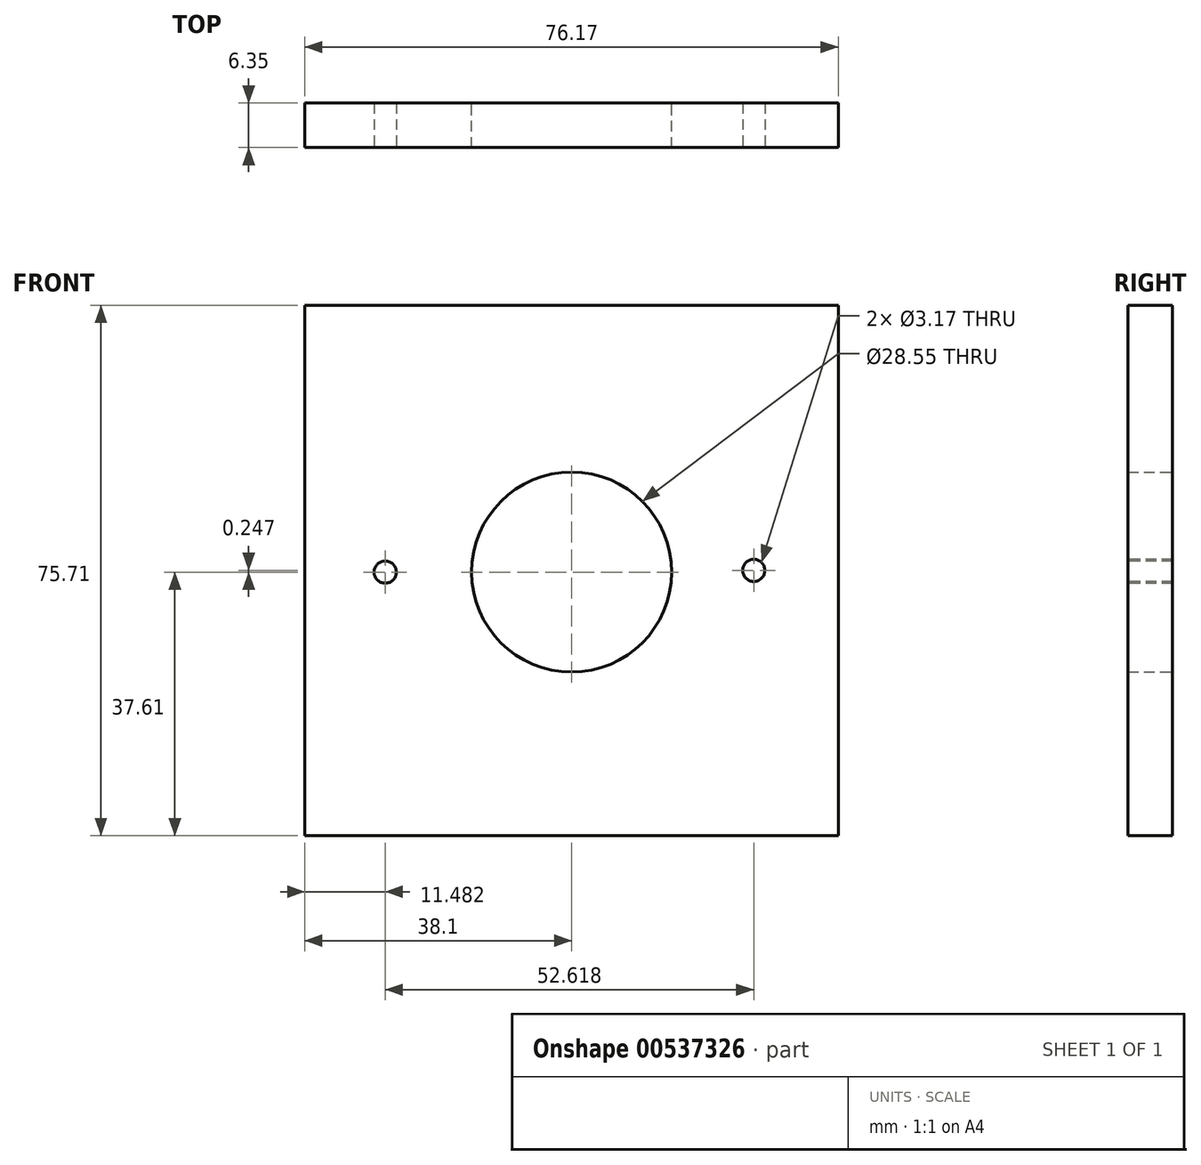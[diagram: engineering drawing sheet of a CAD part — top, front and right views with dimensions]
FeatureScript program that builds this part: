
annotation { "Feature Type Name" : "Feature", "Feature Type Description" : "" }
export const myFeature = defineFeature(function(context is Context, id is Id, definition is map)
    precondition{}
    {
        {
            var Q0;
            Q0=qCreatedBy(makeId("Front.planeOp"),FACE);
            var sketch = newSketch(context, id + "F0", { "sketchPlane" : qUnion([Q0])});
            skCircle(sketch, "E0", {"center": v(0, 0) * mm, "radius": 14.27 * mm});
            skLineSegment(sketch, "E1", {"start": v(-14.27, 0) * mm, "end": v(-38.1, 0) * mm, "construction": true});
            skLineSegment(sketch, "E2", {"start": v(14.27, 0) * mm, "end": v(38.1, 0) * mm, "construction": true});
            skLineSegment(sketch, "E3", {"start": v(0, 14.27) * mm, "end": v(0, 38.1) * mm, "construction": true});
            skLineSegment(sketch, "E4", {"start": v(0, -14.27) * mm, "end": v(0, -38.1) * mm, "construction": true});
            skLineSegment(sketch, "E5.bottom", {"start": v(-38.1, 38.1) * mm, "end": v(38.07, 38.1) * mm});
            skLineSegment(sketch, "E5.top", {"start": v(-38.1, -37.6) * mm, "end": v(38.07, -37.6) * mm});
            skLineSegment(sketch, "E5.left", {"start": v(-38.1, 38.1) * mm, "end": v(-38.1, -37.6) * mm});
            skLineSegment(sketch, "E5.right", {"start": v(38.07, 38.1) * mm, "end": v(38.07, -37.6) * mm});
            skSolve(sketch);
        }
        {
            var Q0;
            Q0=makeQuery(id+"F0.imprint","IMPRINT",FACE,{"disambiguationData":[TD([[makeQuery(id+"F0.imprint","IMPRINT",EDGE,{"derivedFrom":sQuery(id+"F0.wireOp",EDGE,"E0")}),-1.0]])]});
            extrude(context, id + "F1", {"entities" : qUnion([Q0]), "flatOperationType" : FlatOperationType.REMOVE, "depth" : 6.35 * mm, "offsetDistance" : 25.4 * mm, "domain" : OperationDomain.MODEL});
        }
        {
            var Q0;
            Q0=makeQuery(id+"F1.opExtrude","CAP_FACE",FACE,{"disambiguationData":[OSD([sQuery(id+"F0.wireOp",EDGE,"E0"),sQuery(id+"F0.wireOp",EDGE,"E5.bottom"),sQuery(id+"F0.wireOp",EDGE,"E5.top"),sQuery(id+"F0.wireOp",EDGE,"E5.left"),sQuery(id+"F0.wireOp",EDGE,"E5.right")])],"isStart":false});
            var sketch = newSketch(context, id + "F2", { "sketchPlane" : qUnion([Q0])});
            skLineSegment(sketch, "E6", {"start": v(-14.27, 0) * mm, "end": v(-24.6, 0) * mm});
            skPoint(sketch, "E7.startSnap0", {"position": v(-38.1, 0.25) * mm});
            skLineSegment(sketch, "E8", {"start": v(-27.77, 0.25) * mm, "end": v(-38.1, 0.25) * mm, "construction": true});
            skCircle(sketch, "E9", {"center": v(-26.62, 0) * mm, "radius": 1.59 * mm});
            skLineSegment(sketch, "E10", {"start": v(14.27, 0) * mm, "end": v(24.6, 0) * mm, "construction": true});
            skLineSegment(sketch, "E11", {"start": v(27.75, 0.25) * mm, "end": v(38.07, 0) * mm, "construction": true});
            skPoint(sketch, "E11.startSnap0", {"position": v(38.07, 0.25) * mm});
            skPoint(sketch, "E11.endSnap0", {"position": v(38.07, 0.25) * mm});
            skCircle(sketch, "E12", {"center": v(26.3, 0) * mm, "radius": 1.59 * mm});
            skSolve(sketch);
        }
        {
            var Q0;
            Q0=makeQuery(id+"F2.imprint","IMPRINT",FACE,{"disambiguationData":[TD([[makeQuery(id+"F2.imprint","IMPRINT",EDGE,{"derivedFrom":sQuery(id+"F2.wireOp",EDGE,"E9")}),1.0]])]});
            extrude(context, id + "F3", {"entities" : qUnion([Q0]), "operationType" : NewBodyOperationType.REMOVE, "oppositeDirection" : true, "depth" : 6.35 * mm, "offsetDistance" : 25.4 * mm});
        }
        {
            var Q0;
            Q0=makeQuery(id+"F1.opExtrude","CAP_FACE",FACE,{"disambiguationData":[OSD([sQuery(id+"F0.wireOp",EDGE,"E0"),sQuery(id+"F0.wireOp",EDGE,"E5.bottom"),sQuery(id+"F0.wireOp",EDGE,"E5.top"),sQuery(id+"F0.wireOp",EDGE,"E5.left"),sQuery(id+"F0.wireOp",EDGE,"E5.right")])],"isStart":false});
            var sketch = newSketch(context, id + "F4", { "sketchPlane" : qUnion([Q0])});
            skLineSegment(sketch, "E13", {"start": v(14.27, 0) * mm, "end": v(24.6, 0) * mm, "construction": true});
            skLineSegment(sketch, "E14", {"start": v(38.07, 0.25) * mm, "end": v(27.75, 0.25) * mm, "construction": true});
            skCircle(sketch, "E15", {"center": v(26, 0.25) * mm, "radius": 1.59 * mm});
            skSolve(sketch);
        }
        {
            var Q0;
            Q0=makeQuery(id+"F4.imprint","IMPRINT",FACE,{"disambiguationData":[TD([[makeQuery(id+"F4.imprint","IMPRINT",EDGE,{"derivedFrom":sQuery(id+"F4.wireOp",EDGE,"E15")}),1.0]])]});
            extrude(context, id + "F5", {"entities" : qUnion([Q0]), "operationType" : NewBodyOperationType.REMOVE, "oppositeDirection" : true, "depth" : 6.35 * mm, "offsetDistance" : 25.4 * mm});
        }
    });
